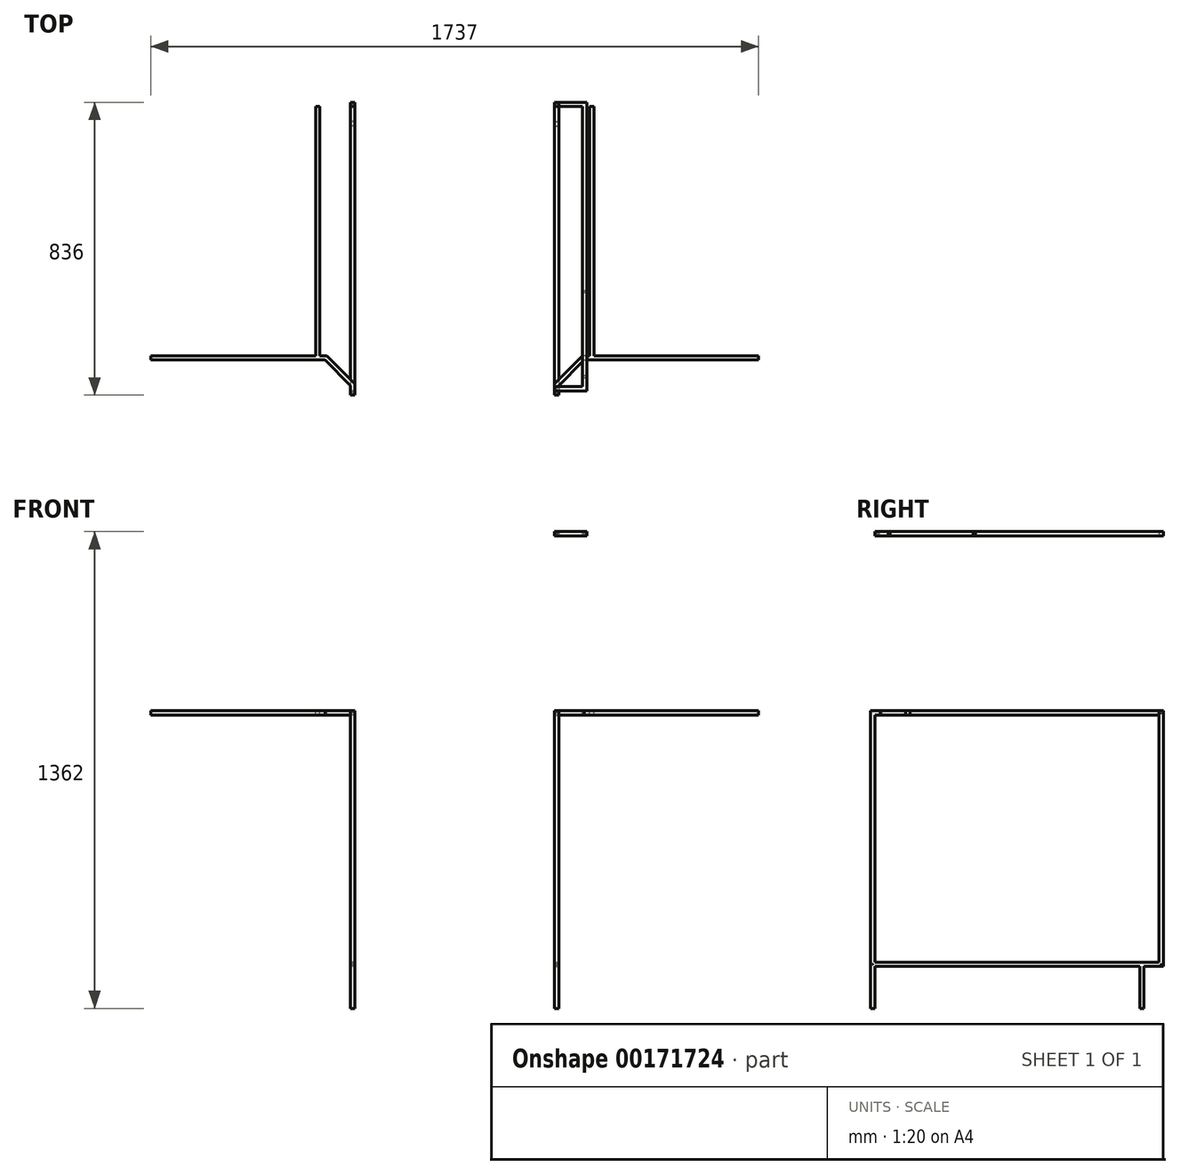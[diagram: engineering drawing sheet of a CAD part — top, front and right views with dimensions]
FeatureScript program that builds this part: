
annotation { "Feature Type Name" : "Feature", "Feature Type Description" : "" }
export const myFeature = defineFeature(function(context is Context, id is Id, definition is map)
    precondition{}
    {
        {
            var Q0;
            Q0=qCreatedBy(makeId("Right.planeOp"),FACE);
            var sketch = newSketch(context, id + "F0", { "sketchPlane" : qUnion([Q0])});
            skLineSegment(sketch, "E0.bottom", {"start": v(418, -365) * mm, "end": v(-418, -365) * mm});
            skLineSegment(sketch, "E0.top", {"start": v(418, 365) * mm, "end": v(-418, 365) * mm});
            skLineSegment(sketch, "E0.left", {"start": v(418, -365) * mm, "end": v(418, 365) * mm});
            skLineSegment(sketch, "E0.right", {"start": v(-418, -365) * mm, "end": v(-418, 365) * mm});
            skPoint(sketch, "E0.middle", {"position": v(0, 0) * mm});
            skLineSegment(sketch, "E1.0", {"start": v(406, 353) * mm, "end": v(-406, 353) * mm});
            skLineSegment(sketch, "E1.1", {"start": v(406, -353) * mm, "end": v(406, 353) * mm});
            skLineSegment(sketch, "E1.2", {"start": v(406, -353) * mm, "end": v(-406, -353) * mm});
            skLineSegment(sketch, "E1.3", {"start": v(-406, -353) * mm, "end": v(-406, 353) * mm});
            skLineSegment(sketch, "E2.bottom", {"start": v(-418, -365) * mm, "end": v(-406, -365) * mm});
            skLineSegment(sketch, "E2.top", {"start": v(-418, -485) * mm, "end": v(-406, -485) * mm});
            skLineSegment(sketch, "E2.left", {"start": v(-418, -365) * mm, "end": v(-418, -485) * mm});
            skLineSegment(sketch, "E2.right", {"start": v(-406, -365) * mm, "end": v(-406, -485) * mm});
            skPoint(sketch, "E3", {"position": v(363, -365) * mm});
            skLineSegment(sketch, "E4.bottom", {"start": v(363, -365) * mm, "end": v(351, -365) * mm});
            skLineSegment(sketch, "E4.top", {"start": v(363, -485) * mm, "end": v(351, -485) * mm});
            skLineSegment(sketch, "E4.left", {"start": v(363, -365) * mm, "end": v(363, -485) * mm});
            skLineSegment(sketch, "E4.right", {"start": v(351, -365) * mm, "end": v(351, -485) * mm});
            skLineSegment(sketch, "E5.bottom", {"start": v(-406, -353) * mm, "end": v(-418, -353) * mm});
            skLineSegment(sketch, "E5.top", {"start": v(-406, -365) * mm, "end": v(-418, -365) * mm});
            skLineSegment(sketch, "E5.left", {"start": v(-406, -353) * mm, "end": v(-406, -365) * mm});
            skLineSegment(sketch, "E5.right", {"start": v(-418, -353) * mm, "end": v(-418, -365) * mm});
            skPoint(sketch, "E6", {"position": v(-412, -359) * mm});
            skLineSegment(sketch, "E7.bottom", {"start": v(406, -353) * mm, "end": v(418, -353) * mm});
            skLineSegment(sketch, "E7.top", {"start": v(406, -365) * mm, "end": v(418, -365) * mm});
            skLineSegment(sketch, "E7.left", {"start": v(406, -353) * mm, "end": v(406, -365) * mm});
            skLineSegment(sketch, "E7.right", {"start": v(418, -353) * mm, "end": v(418, -365) * mm});
            skPoint(sketch, "E8", {"position": v(412, -359) * mm});
            skLineSegment(sketch, "E9.bottom", {"start": v(418, 365) * mm, "end": v(406, 365) * mm});
            skLineSegment(sketch, "E9.top", {"start": v(418, 353) * mm, "end": v(406, 353) * mm});
            skLineSegment(sketch, "E9.left", {"start": v(418, 365) * mm, "end": v(418, 353) * mm});
            skLineSegment(sketch, "E9.right", {"start": v(406, 365) * mm, "end": v(406, 353) * mm});
            skPoint(sketch, "E10", {"position": v(412, 359) * mm});
            skLineSegment(sketch, "E11.bottom", {"start": v(-318, 365) * mm, "end": v(-306, 365) * mm});
            skLineSegment(sketch, "E11.top", {"start": v(-318, 353) * mm, "end": v(-306, 353) * mm});
            skLineSegment(sketch, "E11.left", {"start": v(-318, 365) * mm, "end": v(-318, 353) * mm});
            skLineSegment(sketch, "E11.right", {"start": v(-306, 365) * mm, "end": v(-306, 353) * mm});
            skPoint(sketch, "E12", {"position": v(-312, 359) * mm});
            skSolve(sketch);
        }
        {
            var Q0;
            Q0=qSketchRegion(id+"F0",true);
            extrude(context, id + "F1", {"entities" : qUnion([Q0]), "depth" : 12 * mm});
        }
        {
            var Q0;
            Q0=makeQuery(id+"F1.opExtrude","CAP_FACE",FACE,{"disambiguationData":[OSD([sQuery(id+"F0.wireOp",EDGE,"E0.bottom"),sQuery(id+"F0.wireOp",EDGE,"E0.top"),sQuery(id+"F0.wireOp",EDGE,"E0.left"),sQuery(id+"F0.wireOp",EDGE,"E0.right"),sQuery(id+"F0.wireOp",EDGE,"E1.0"),sQuery(id+"F0.wireOp",EDGE,"E1.1"),sQuery(id+"F0.wireOp",EDGE,"E1.2"),sQuery(id+"F0.wireOp",EDGE,"E1.3"),sQuery(id+"F0.wireOp",EDGE,"E2.top"),sQuery(id+"F0.wireOp",EDGE,"E2.left"),sQuery(id+"F0.wireOp",EDGE,"E2.right"),sQuery(id+"F0.wireOp",EDGE,"E4.top"),sQuery(id+"F0.wireOp",EDGE,"E4.left"),sQuery(id+"F0.wireOp",EDGE,"E4.right"),sQuery(id+"F0.wireOp",EDGE,"E5.right"),sQuery(id+"F0.wireOp",EDGE,"E7.top"),sQuery(id+"F0.wireOp",EDGE,"E7.right"),sQuery(id+"F0.wireOp",EDGE,"E9.bottom"),sQuery(id+"F0.wireOp",EDGE,"E9.left"),sQuery(id+"F0.wireOp",EDGE,"E11.bottom"),sQuery(id+"F0.wireOp",EDGE,"E11.top")])],"isStart":false});
            var sketch = newSketch(context, id + "F2", { "sketchPlane" : qUnion([Q0])});
            skLineSegment(sketch, "E13.0.0", {"start": v(406, -353) * mm, "end": v(406, 353) * mm});
            skLineSegment(sketch, "E13.0.1", {"start": v(406, 353) * mm, "end": v(-306, 353) * mm});
            skLineSegment(sketch, "E13.0.2", {"start": v(-306, 353) * mm, "end": v(-318, 353) * mm});
            skLineSegment(sketch, "E13.0.3", {"start": v(-318, 353) * mm, "end": v(-406, 353) * mm});
            skLineSegment(sketch, "E13.0.4", {"start": v(-406, 353) * mm, "end": v(-406, -353) * mm});
            skLineSegment(sketch, "E13.0.5", {"start": v(-406, -353) * mm, "end": v(406, -353) * mm});
            skPoint(sketch, "E14.0", {"position": v(-312, 359) * mm});
            skLineSegment(sketch, "E15.0", {"start": v(406, 353) * mm, "end": v(-406, 353) * mm});
            skLineSegment(sketch, "E16.0", {"start": v(-306, 365) * mm, "end": v(-306, 353) * mm});
            skLineSegment(sketch, "E17.0", {"start": v(418, 365) * mm, "end": v(-418, 365) * mm});
            skLineSegment(sketch, "E18.0", {"start": v(-318, 365) * mm, "end": v(-318, 353) * mm});
            skLineSegment(sketch, "E19.0", {"start": v(-418, -365) * mm, "end": v(-418, 365) * mm});
            skLineSegment(sketch, "E20.0", {"start": v(-406, -353) * mm, "end": v(-406, 353) * mm});
            skLineSegment(sketch, "E21.0", {"start": v(-418, -365) * mm, "end": v(-418, -485) * mm});
            skLineSegment(sketch, "E22.0", {"start": v(-406, -365) * mm, "end": v(-406, -485) * mm});
            skLineSegment(sketch, "E23.0", {"start": v(418, -365) * mm, "end": v(-418, -365) * mm});
            skLineSegment(sketch, "E24.0", {"start": v(406, -353) * mm, "end": v(-406, -353) * mm});
            skLineSegment(sketch, "E25.0", {"start": v(-406, -353) * mm, "end": v(-418, -353) * mm});
            skLineSegment(sketch, "E26.0", {"start": v(-406, -353) * mm, "end": v(-406, -365) * mm});
            skPoint(sketch, "E27.0", {"position": v(-412, -359) * mm});
            skLineSegment(sketch, "E28.0", {"start": v(351, -365) * mm, "end": v(351, -485) * mm});
            skLineSegment(sketch, "E29.0", {"start": v(363, -365) * mm, "end": v(363, -485) * mm});
            skLineSegment(sketch, "E30.0", {"start": v(363, -485) * mm, "end": v(351, -485) * mm});
            skLineSegment(sketch, "E31.0.0", {"start": v(418, -353) * mm, "end": v(406, -353) * mm});
            skLineSegment(sketch, "E31.0.1", {"start": v(406, -353) * mm, "end": v(406, -365) * mm});
            skLineSegment(sketch, "E31.0.2", {"start": v(406, -365) * mm, "end": v(418, -365) * mm});
            skLineSegment(sketch, "E31.0.3", {"start": v(418, -365) * mm, "end": v(418, -353) * mm});
            skPoint(sketch, "E32.0", {"position": v(412, -359) * mm});
            skLineSegment(sketch, "E33.0", {"start": v(418, -365) * mm, "end": v(418, 365) * mm});
            skLineSegment(sketch, "E34.0.0", {"start": v(418, 353) * mm, "end": v(418, 365) * mm});
            skLineSegment(sketch, "E34.0.1", {"start": v(418, 365) * mm, "end": v(406, 365) * mm});
            skLineSegment(sketch, "E34.0.2", {"start": v(406, 365) * mm, "end": v(406, 353) * mm});
            skLineSegment(sketch, "E34.0.3", {"start": v(406, 353) * mm, "end": v(418, 353) * mm});
            skPoint(sketch, "E35.0", {"position": v(412, 359) * mm});
            skSolve(sketch);
        }
        {
            var Q0;
            Q0=sQuery(id+"F0.wireOp",VERTEX,"E10");
            var Q1;
            Q1=sQuery(id+"F0.wireOp",VERTEX,"E8");
            var Q2;
            Q2=sQuery(id+"F0.wireOp",VERTEX,"E6");
            var Q3;
            Q3=sQuery(id+"F0.wireOp",VERTEX,"E12");
            var Q4;
            Q4=makeQuery(id+"F1.opExtrude","SWEPT_BODY",BODY,{"disambiguationData":[OSD([sQuery(id+"F0.wireOp",EDGE,"E0.bottom"),sQuery(id+"F0.wireOp",EDGE,"E0.top"),sQuery(id+"F0.wireOp",EDGE,"E0.left"),sQuery(id+"F0.wireOp",EDGE,"E0.right"),sQuery(id+"F0.wireOp",EDGE,"E1.0"),sQuery(id+"F0.wireOp",EDGE,"E1.1"),sQuery(id+"F0.wireOp",EDGE,"E1.2"),sQuery(id+"F0.wireOp",EDGE,"E1.3"),sQuery(id+"F0.wireOp",EDGE,"E2.top"),sQuery(id+"F0.wireOp",EDGE,"E2.left"),sQuery(id+"F0.wireOp",EDGE,"E2.right"),sQuery(id+"F0.wireOp",EDGE,"E4.top"),sQuery(id+"F0.wireOp",EDGE,"E4.left"),sQuery(id+"F0.wireOp",EDGE,"E4.right"),sQuery(id+"F0.wireOp",EDGE,"E5.right"),sQuery(id+"F0.wireOp",EDGE,"E7.top"),sQuery(id+"F0.wireOp",EDGE,"E7.right"),sQuery(id+"F0.wireOp",EDGE,"E9.bottom"),sQuery(id+"F0.wireOp",EDGE,"E9.left"),sQuery(id+"F0.wireOp",EDGE,"E11.bottom"),sQuery(id+"F0.wireOp",EDGE,"E11.top")])]});
            hole(context, id + "F3", {"style" : HoleStyle.C_SINK, "endStyle" : HoleEndStyle.BLIND, "oppositeDirection" : true, "holeDiameter" : 0.5 * mm, "cSinkDiameter" : 0.5 * mm, "cSinkAngle" : 90 * degree, "holeDepth" : 12 * mm, "startFromSketch" : true, "locations" : qUnion([Q0, Q1, Q2, Q3]), "scope" : qUnion([Q4])});
        }
        {
            var Q0;
            Q0=makeQuery(id+"F1.opExtrude","SWEPT_FACE",FACE,{"disambiguationData":[OSD([sQuery(id+"F0.wireOp",EDGE,"E0.top"),sQuery(id+"F0.wireOp",EDGE,"E9.bottom"),sQuery(id+"F0.wireOp",EDGE,"E11.bottom")])]});
            var sketch = newSketch(context, id + "F4", { "sketchPlane" : qUnion([Q0])});
            skLineSegment(sketch, "E36.0", {"start": v(12, -418) * mm, "end": v(0, -418) * mm});
            skLineSegment(sketch, "E37.0", {"start": v(0, -406) * mm, "end": v(0, -418) * mm});
            skLineSegment(sketch, "E38.0", {"start": v(12, -386) * mm, "end": v(12, -418) * mm});
            skPoint(sketch, "E39", {"position": v(12, -386) * mm});
            skLineSegment(sketch, "E40", {"start": v(12, -386) * mm, "end": v(0, -390.97) * mm});
            skLineSegment(sketch, "E41", {"start": v(-571, -318) * mm, "end": v(-571, -306) * mm});
            skLineSegment(sketch, "E42", {"start": v(-571, -306) * mm, "end": v(-68, -306) * mm});
            skLineSegment(sketch, "E43", {"start": v(12, -386) * mm, "end": v(-68, -306) * mm});
            skLineSegment(sketch, "E44", {"start": v(0, -390.97) * mm, "end": v(-72.97, -318) * mm});
            skLineSegment(sketch, "E45", {"start": v(-72.97, -318) * mm, "end": v(-68, -306) * mm});
            skLineSegment(sketch, "E46.trimOffspring", {"start": v(-72.97, -318) * mm, "end": v(-571, -318) * mm});
            skLineSegment(sketch, "E47.trimOffspring", {"start": v(0, -374) * mm, "end": v(0, -406) * mm});
            skPoint(sketch, "E48.orphan", {"position": v(0, 406) * mm});
            skPoint(sketch, "E49.orphan", {"position": v(12, 418) * mm});
            skLineSegment(sketch, "E50", {"start": v(12, -386) * mm, "end": v(12, -256.08) * mm, "construction": true});
            skPoint(sketch, "E51.0", {"position": v(12, 406) * mm});
            skLineSegment(sketch, "E52.0.0", {"start": v(0, 418) * mm, "end": v(0, -418) * mm});
            skLineSegment(sketch, "E52.0.1", {"start": v(0, -418) * mm, "end": v(12, -418) * mm});
            skLineSegment(sketch, "E52.0.2", {"start": v(12, -418) * mm, "end": v(12, 418) * mm});
            skLineSegment(sketch, "E52.0.3", {"start": v(12, 418) * mm, "end": v(0, 418) * mm});
            skLineSegment(sketch, "E53", {"start": v(12, 406) * mm, "end": v(0, 406) * mm});
            skLineSegment(sketch, "E54", {"start": v(0, 406) * mm, "end": v(-176, 406) * mm, "construction": true});
            skPoint(sketch, "E55", {"position": v(-88, 406) * mm});
            skLineSegment(sketch, "E56.bottom", {"start": v(-88, 406) * mm, "end": v(-100, 406) * mm});
            skLineSegment(sketch, "E56.top", {"start": v(-88, -306) * mm, "end": v(-100, -306) * mm});
            skLineSegment(sketch, "E56.left", {"start": v(-88, 406) * mm, "end": v(-88, -306) * mm});
            skLineSegment(sketch, "E56.right", {"start": v(-100, 406) * mm, "end": v(-100, -306) * mm});
            skSolve(sketch);
        }
        {
            var Q0;
            Q0=makeQuery(id+"F4.imprint","IMPRINT",FACE,{"disambiguationData":[TD([[makeQuery(id+"F4.imprint","IMPRINT",EDGE,{"derivedFrom":sQuery(id+"F4.wireOp",EDGE,"E56.bottom")}),1.0]])]});
            var Q1;
            {var subQ4=sQuery(id+"F4.wireOp",EDGE,"E44");Q1=makeQuery(id+"F4.imprint","IMPRINT",FACE,{"disambiguationData":[TD([[makeQuery(id+"F4.imprint","IMPRINT",EDGE,{"derivedFrom":subQ4}),-1.0]])]});}
            var Q2;
            {var subQ2=sQuery(id+"F4.wireOp",EDGE,"E41");Q2=makeQuery(id+"F4.imprint","IMPRINT",FACE,{"disambiguationData":[TD([[makeQuery(id+"F4.imprint","IMPRINT",EDGE,{"derivedFrom":subQ2}),-1.0]])]});}
            extrude(context, id + "F5", {"entities" : qUnion([Q0, Q1, Q2]), "operationType" : NewBodyOperationType.ADD, "oppositeDirection" : true, "depth" : 12 * mm});
        }
        {
            var Q0;
            {var subQ5=sQuery(id+"F4.wireOp",EDGE,"E53");Q0=makeQuery(id+"F4.imprint","IMPRINT",FACE,{"disambiguationData":[TD([[makeQuery(id+"F4.imprint","IMPRINT",EDGE,{"derivedFrom":subQ5}),1.0]])]});}
            extrude(context, id + "F6", {"entities" : qUnion([Q0]), "operationType" : NewBodyOperationType.REMOVE, "oppositeDirection" : true, "depth" : 12 * mm});
        }
        {
            var Q0;
            Q0=qCreatedBy(makeId("Right.planeOp"),FACE);
            cPlane(context, id + "F7", {"entities" : qUnion([Q0]), "cplaneType" : CPlaneType.OFFSET, "offset" : 297.5 * mm, "width" : 150 * mm, "height" : 150 * mm});
        }
        {
            var Q0;
            Q0=makeQuery(id+"F1.opExtrude","SWEPT_BODY",BODY,{"disambiguationData":[OSD([sQuery(id+"F0.wireOp",EDGE,"E0.bottom"),sQuery(id+"F0.wireOp",EDGE,"E0.top"),sQuery(id+"F0.wireOp",EDGE,"E0.left"),sQuery(id+"F0.wireOp",EDGE,"E0.right"),sQuery(id+"F0.wireOp",EDGE,"E1.0"),sQuery(id+"F0.wireOp",EDGE,"E1.1"),sQuery(id+"F0.wireOp",EDGE,"E1.2"),sQuery(id+"F0.wireOp",EDGE,"E1.3"),sQuery(id+"F0.wireOp",EDGE,"E2.top"),sQuery(id+"F0.wireOp",EDGE,"E2.left"),sQuery(id+"F0.wireOp",EDGE,"E2.right"),sQuery(id+"F0.wireOp",EDGE,"E4.top"),sQuery(id+"F0.wireOp",EDGE,"E4.left"),sQuery(id+"F0.wireOp",EDGE,"E4.right"),sQuery(id+"F0.wireOp",EDGE,"E5.right"),sQuery(id+"F0.wireOp",EDGE,"E7.top"),sQuery(id+"F0.wireOp",EDGE,"E7.right"),sQuery(id+"F0.wireOp",EDGE,"E9.bottom"),sQuery(id+"F0.wireOp",EDGE,"E9.left"),sQuery(id+"F0.wireOp",EDGE,"E11.bottom"),sQuery(id+"F0.wireOp",EDGE,"E11.top")])]});
            var Q1;
            Q1=qCreatedBy(id+"F7.planeOp",FACE);
            mirror(context, id + "F8", {"entities" : qUnion([Q0]), "mirrorPlane" : qUnion([Q1])});
        }
        {
            var Q0;
            {var subQ0=sQuery(id+"F4.wireOp",EDGE,"E56.bottom");var subQ1=sQuery(id+"F4.wireOp",EDGE,"E46.trimOffspring");var subQ2=sQuery(id+"F4.wireOp",EDGE,"E42");var subQ3=sQuery(id+"F4.wireOp",EDGE,"E41");var subQ4=sQuery(id+"F4.wireOp",EDGE,"E56.right");var subQ7=sQuery(id+"F0.wireOp",EDGE,"E11.bottom");var subQ9=sQuery(id+"F0.wireOp",EDGE,"E9.bottom");var subQ25=sQuery(id+"F0.wireOp",EDGE,"E0.top");var subQ27=sQuery(id+"F4.wireOp",EDGE,"E43");var subQ28=sQuery(id+"F4.wireOp",EDGE,"E56.left");var subQ29=sQuery(id+"F4.wireOp",EDGE,"E44");Q0=makeQuery(id+"F8.opPattern","COPY",FACE,{"derivedFrom":makeQuery(id+"F6.boolean.opBoolean","SPLIT",FACE,{"disambiguationData":[TD([makeQuery(id+"F5.opExtrude","SWEPT_FACE",FACE,{"disambiguationData":[OSD([subQ3])]})])],"derivedFrom":makeQuery(id+"F5.boolean.opBoolean","MERGE",FACE,{"derivedFrom":[makeQuery(id+"F1.opExtrude","SWEPT_FACE",FACE,{"disambiguationData":[OSD([subQ25,subQ9,subQ7])]}),makeQuery(id+"F5.opExtrude","CAP_FACE",FACE,{"disambiguationData":[OSD([subQ3,subQ2,subQ27,subQ29,subQ1,sQuery(id+"F4.wireOp",EDGE,"E52.0.0"),subQ0,subQ28,subQ4])],"isStart":true})]})}),"instanceName":"1"});}
            var sketch = newSketch(context, id + "F9", { "sketchPlane" : qUnion([Q0])});
            skLineSegment(sketch, "E57.0.1", {"start": v(583, -418) * mm, "end": v(595, -418) * mm});
            skLineSegment(sketch, "E57.0.4", {"start": v(667.97, -318) * mm, "end": v(1166, -318) * mm});
            skLineSegment(sketch, "E57.0.5", {"start": v(1166, -318) * mm, "end": v(1166, -306) * mm});
            skLineSegment(sketch, "E57.0.6", {"start": v(1166, -306) * mm, "end": v(695, -306) * mm});
            skLineSegment(sketch, "E57.0.7", {"start": v(695, -306) * mm, "end": v(695, 406) * mm});
            skLineSegment(sketch, "E57.0.8", {"start": v(695, 406) * mm, "end": v(683, 406) * mm});
            skLineSegment(sketch, "E57.0.9", {"start": v(683, 406) * mm, "end": v(683, -306) * mm});
            skLineSegment(sketch, "E57.0.10", {"start": v(683, -306) * mm, "end": v(663, -306) * mm});
            skPoint(sketch, "E58.end.orphan", {"position": v(583, -394) * mm});
            skLineSegment(sketch, "E59", {"start": v(583, -394) * mm, "end": v(583, -418) * mm});
            skLineSegment(sketch, "E60", {"start": v(583, -394) * mm, "end": v(663, -394) * mm});
            skLineSegment(sketch, "E61", {"start": v(663, -394) * mm, "end": v(663, 406) * mm});
            skLineSegment(sketch, "E62", {"start": v(675, 405) * mm, "end": v(675, -406) * mm});
            skLineSegment(sketch, "E63", {"start": v(675, -406) * mm, "end": v(595, -406) * mm});
            skLineSegment(sketch, "E64", {"start": v(595, -406) * mm, "end": v(595, -418) * mm});
            skPoint(sketch, "E65.0", {"position": v(595, 406) * mm});
            skPoint(sketch, "E66.0", {"position": v(595, 418) * mm});
            skLineSegment(sketch, "E67", {"start": v(663, 406) * mm, "end": v(595, 406) * mm});
            skLineSegment(sketch, "E68", {"start": v(595, 406) * mm, "end": v(595, 418) * mm});
            skLineSegment(sketch, "E69", {"start": v(675, 418) * mm, "end": v(595, 418) * mm});
            skLineSegment(sketch, "E70", {"start": v(675, 418) * mm, "end": v(675, 405) * mm});
            skLineSegment(sketch, "E71", {"start": v(595, -406) * mm, "end": v(583, -406) * mm});
            skSolve(sketch);
        }
        {
            var Q0;
            {var subQ0=sQuery(id+"F9.wireOp",EDGE,"E67");Q0=makeQuery(id+"F9.imprint","IMPRINT",FACE,{"disambiguationData":[TD([[makeQuery(id+"F9.imprint","IMPRINT",EDGE,{"derivedFrom":subQ0}),-1.0]])]});}
            cPlane(context, id + "F10", {"entities" : qUnion([Q0]), "cplaneType" : CPlaneType.OFFSET, "offset" : 500 * mm, "width" : 150 * mm, "height" : 150 * mm});
        }
        {
            var Q0;
            Q0=qCreatedBy(id+"F10.planeOp",FACE);
            var sketch = newSketch(context, id + "F11", { "sketchPlane" : qUnion([Q0])});
            skLineSegment(sketch, "E72.0", {"start": v(583, -394) * mm, "end": v(583, -418) * mm});
            skLineSegment(sketch, "E73.0", {"start": v(583, -418) * mm, "end": v(595, -418) * mm});
            skLineSegment(sketch, "E74.0", {"start": v(595, -406) * mm, "end": v(595, -418) * mm});
            skLineSegment(sketch, "E75.0", {"start": v(675, -406) * mm, "end": v(595, -406) * mm});
            skLineSegment(sketch, "E76.0", {"start": v(583, -394) * mm, "end": v(663, -394) * mm});
            skLineSegment(sketch, "E77.0", {"start": v(663, -394) * mm, "end": v(663, 406) * mm});
            skLineSegment(sketch, "E78.0", {"start": v(675, 405) * mm, "end": v(675, -406) * mm});
            skLineSegment(sketch, "E79.0", {"start": v(675, 418) * mm, "end": v(595, 418) * mm});
            skPoint(sketch, "E80.0", {"position": v(629, 406) * mm});
            skLineSegment(sketch, "E81.0", {"start": v(663, 406) * mm, "end": v(595, 406) * mm});
            skLineSegment(sketch, "E82.0", {"start": v(595, 406) * mm, "end": v(595, 418) * mm});
            skLineSegment(sketch, "E83.0", {"start": v(675, 418) * mm, "end": v(675, 405) * mm});
            skLineSegment(sketch, "E84.0", {"start": v(595, -406) * mm, "end": v(583, -406) * mm});
            skSolve(sketch);
        }
        {
            var Q0;
            Q0=makeQuery(id+"F11.imprint","IMPRINT",FACE,{"disambiguationData":[TD([[makeQuery(id+"F11.imprint","IMPRINT",EDGE,{"derivedFrom":sQuery(id+"F11.wireOp",EDGE,"E75.0")}),-1.0]])]});
            extrude(context, id + "F12", {"entities" : qUnion([Q0]), "depth" : 12 * mm});
        }
        {
            var Q0;
            Q0=makeQuery(id+"F12.opExtrude","SWEPT_FACE",FACE,{"disambiguationData":[OSD([sQuery(id+"F11.wireOp",EDGE,"E75.0"),sQuery(id+"F11.wireOp",EDGE,"E84.0")])]});
            var sketch = newSketch(context, id + "F13", { "sketchPlane" : qUnion([Q0])});
            skLineSegment(sketch, "E85", {"start": v(595, 877) * mm, "end": v(595, 865) * mm});
            skPoint(sketch, "E86", {"position": v(589, 871) * mm});
            skSolve(sketch);
        }
        {
            var Q0;
            Q0=sQuery(id+"F13.wireOp",VERTEX,"E86");
            var Q1;
            Q1=makeQuery(id+"F12.opExtrude","SWEPT_BODY",BODY,{"disambiguationData":[OSD([sQuery(id+"F11.wireOp",EDGE,"E72.0"),sQuery(id+"F11.wireOp",EDGE,"E75.0"),sQuery(id+"F11.wireOp",EDGE,"E76.0"),sQuery(id+"F11.wireOp",EDGE,"E77.0"),sQuery(id+"F11.wireOp",EDGE,"E78.0"),sQuery(id+"F11.wireOp",EDGE,"E79.0"),sQuery(id+"F11.wireOp",EDGE,"E81.0"),sQuery(id+"F11.wireOp",EDGE,"E82.0"),sQuery(id+"F11.wireOp",EDGE,"E83.0"),sQuery(id+"F11.wireOp",EDGE,"E84.0")])]});
            hole(context, id + "F14", {"style" : HoleStyle.C_SINK, "endStyle" : HoleEndStyle.BLIND, "holeDiameter" : 0.5 * mm, "cSinkDiameter" : 0.5 * mm, "cSinkAngle" : 90 * degree, "holeDepth" : 2000 * mm, "startFromSketch" : true, "locations" : qUnion([Q0]), "scope" : qUnion([Q1])});
        }
        {
            var Q0;
            Q0=makeQuery(id+"F12.opExtrude","SWEPT_FACE",FACE,{"disambiguationData":[OSD([sQuery(id+"F11.wireOp",EDGE,"E78.0"),sQuery(id+"F11.wireOp",EDGE,"E83.0")])]});
            var sketch = newSketch(context, id + "F15", { "sketchPlane" : qUnion([Q0])});
            skPoint(sketch, "E87", {"position": v(-365, 871) * mm});
            skPoint(sketch, "E88", {"position": v(-122, 871) * mm});
            skSolve(sketch);
        }
        {
            var Q0;
            Q0=sQuery(id+"F15.wireOp",VERTEX,"E87");
            var Q1;
            Q1=sQuery(id+"F15.wireOp",VERTEX,"E88");
            var Q2;
            Q2=makeQuery(id+"F12.opExtrude","SWEPT_BODY",BODY,{"disambiguationData":[OSD([sQuery(id+"F11.wireOp",EDGE,"E72.0"),sQuery(id+"F11.wireOp",EDGE,"E75.0"),sQuery(id+"F11.wireOp",EDGE,"E76.0"),sQuery(id+"F11.wireOp",EDGE,"E77.0"),sQuery(id+"F11.wireOp",EDGE,"E78.0"),sQuery(id+"F11.wireOp",EDGE,"E79.0"),sQuery(id+"F11.wireOp",EDGE,"E81.0"),sQuery(id+"F11.wireOp",EDGE,"E82.0"),sQuery(id+"F11.wireOp",EDGE,"E83.0"),sQuery(id+"F11.wireOp",EDGE,"E84.0")])]});
            hole(context, id + "F16", {"style" : HoleStyle.C_SINK, "endStyle" : HoleEndStyle.BLIND, "holeDiameter" : 6 * mm, "cSinkDiameter" : 6 * mm, "cSinkAngle" : 90 * degree, "holeDepth" : 20 * mm, "startFromSketch" : true, "locations" : qUnion([Q0, Q1]), "scope" : qUnion([Q2])});
        }
    });
